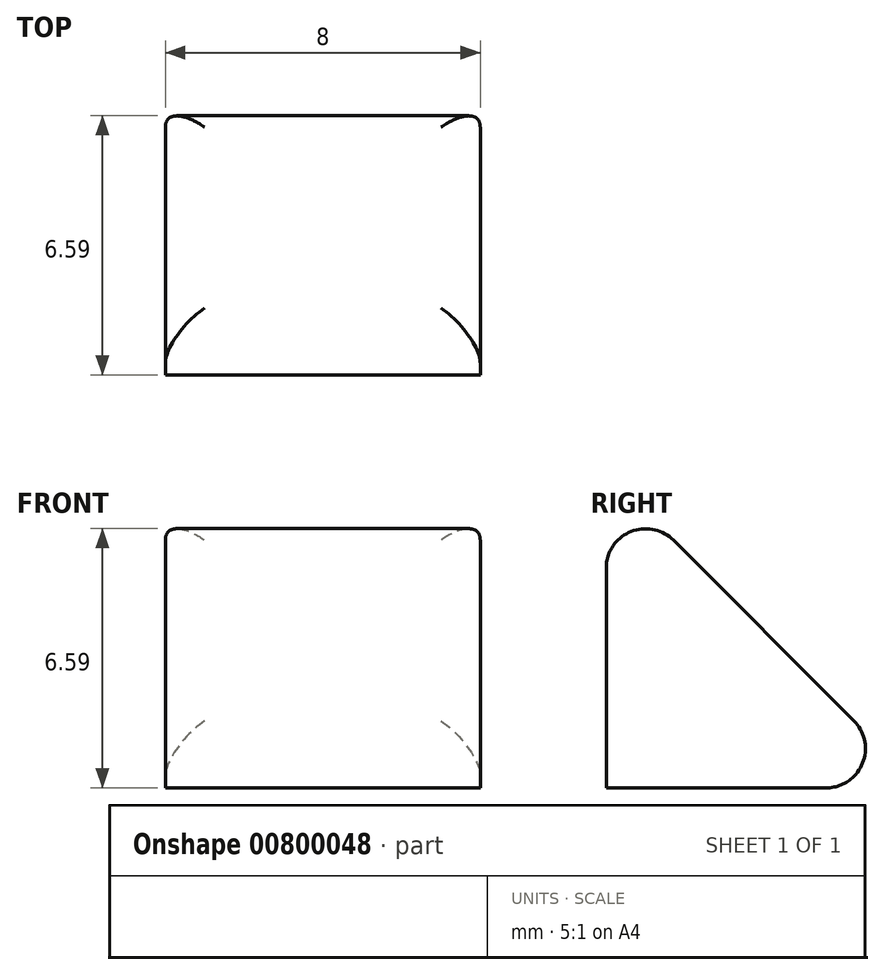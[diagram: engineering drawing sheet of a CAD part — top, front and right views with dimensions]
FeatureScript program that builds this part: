
annotation { "Feature Type Name" : "Feature", "Feature Type Description" : "" }
export const myFeature = defineFeature(function(context is Context, id is Id, definition is map)
    precondition{}
    {
        {
            var Q0;
            Q0=qCreatedBy(makeId("Right.planeOp"),FACE);
            var sketch = newSketch(context, id + "F0", { "sketchPlane" : qUnion([Q0])});
            skLineSegment(sketch, "E0", {"start": v(0, 0) * mm, "end": v(8, 0) * mm});
            skLineSegment(sketch, "E1", {"start": v(8, 0) * mm, "end": v(0, 8) * mm});
            skLineSegment(sketch, "E2", {"start": v(0, 8) * mm, "end": v(0, 0) * mm});
            skSolve(sketch);
        }
        {
            var Q0;
            Q0=makeQuery(id+"F0.imprint","IMPRINT",FACE,{"disambiguationData":[TD([[makeQuery(id+"F0.imprint","IMPRINT",EDGE,{"derivedFrom":sQuery(id+"F0.wireOp",EDGE,"E0")}),1.0]])]});
            extrude(context, id + "F1", {"entities" : qUnion([Q0]), "depth" : 8 * mm, "offsetDistance" : 25 * mm});
        }
        {
            var Q0;
            Q0=makeQuery(id+"F1.opExtrude","SWEPT_EDGE",EDGE,{"disambiguationData":[OSD([sQuery(id+"F0.wireOp",EDGE,"E1"),sQuery(id+"F0.wireOp",EDGE,"E2")])]});
            var Q1;
            Q1=makeQuery(id+"F1.opExtrude","SWEPT_EDGE",EDGE,{"disambiguationData":[OSD([sQuery(id+"F0.wireOp",EDGE,"E0"),sQuery(id+"F0.wireOp",EDGE,"E1")])]});
            var Q2;
            Q2=makeQuery(id+"F1.opExtrude","CAP_EDGE",EDGE,{"disambiguationData":[OSD([sQuery(id+"F0.wireOp",EDGE,"E1")])],"isStart":true});
            var Q3;
            Q3=makeQuery(id+"F1.opExtrude","CAP_EDGE",EDGE,{"disambiguationData":[OSD([sQuery(id+"F0.wireOp",EDGE,"E1")])],"isStart":false});
            fillet(context, id + "F2", {"entities" : qUnion([Q0, Q1, Q2, Q3]), "radius" : 1 * mm, "tangentPropagation" : true, "allowEdgeOverflow" : false});
        }
    });
